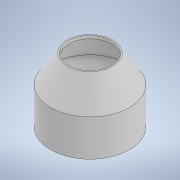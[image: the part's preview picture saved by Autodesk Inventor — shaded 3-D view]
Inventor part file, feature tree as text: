
AUTODESK INVENTOR PART (.ipt)
format: ipt  version: 2022 (Build 260153000, 153)  size: 121,856 bytes
history: native  units: mm
features: sketch x2, extrude x1, revolve x1
ambient origin geometry x8: Origin, YZ Plane, XZ Plane, XY Plane, X Axis, Y Axis, Z Axis, Center Point
bodies: Solid1 (feature_tree)
feature tree (4):
  extrude  "Extrusion1"  Depth=30.0mm
  revolve  "Revolution1"  [1 undecoded]
  sketch  "Sketch1"  dims[d0=32.4mm d1=30.0mm]
  sketch  "Sketch2"  dims[d2=15.0mm d3=0.0mm d7=1.2mm d10=90.0deg]
note: 1 required parameter value undecoded (feature->parameter linkage not recoverable at this tier; creation-order binding heuristic only, values carry confidence <= 0.55)
